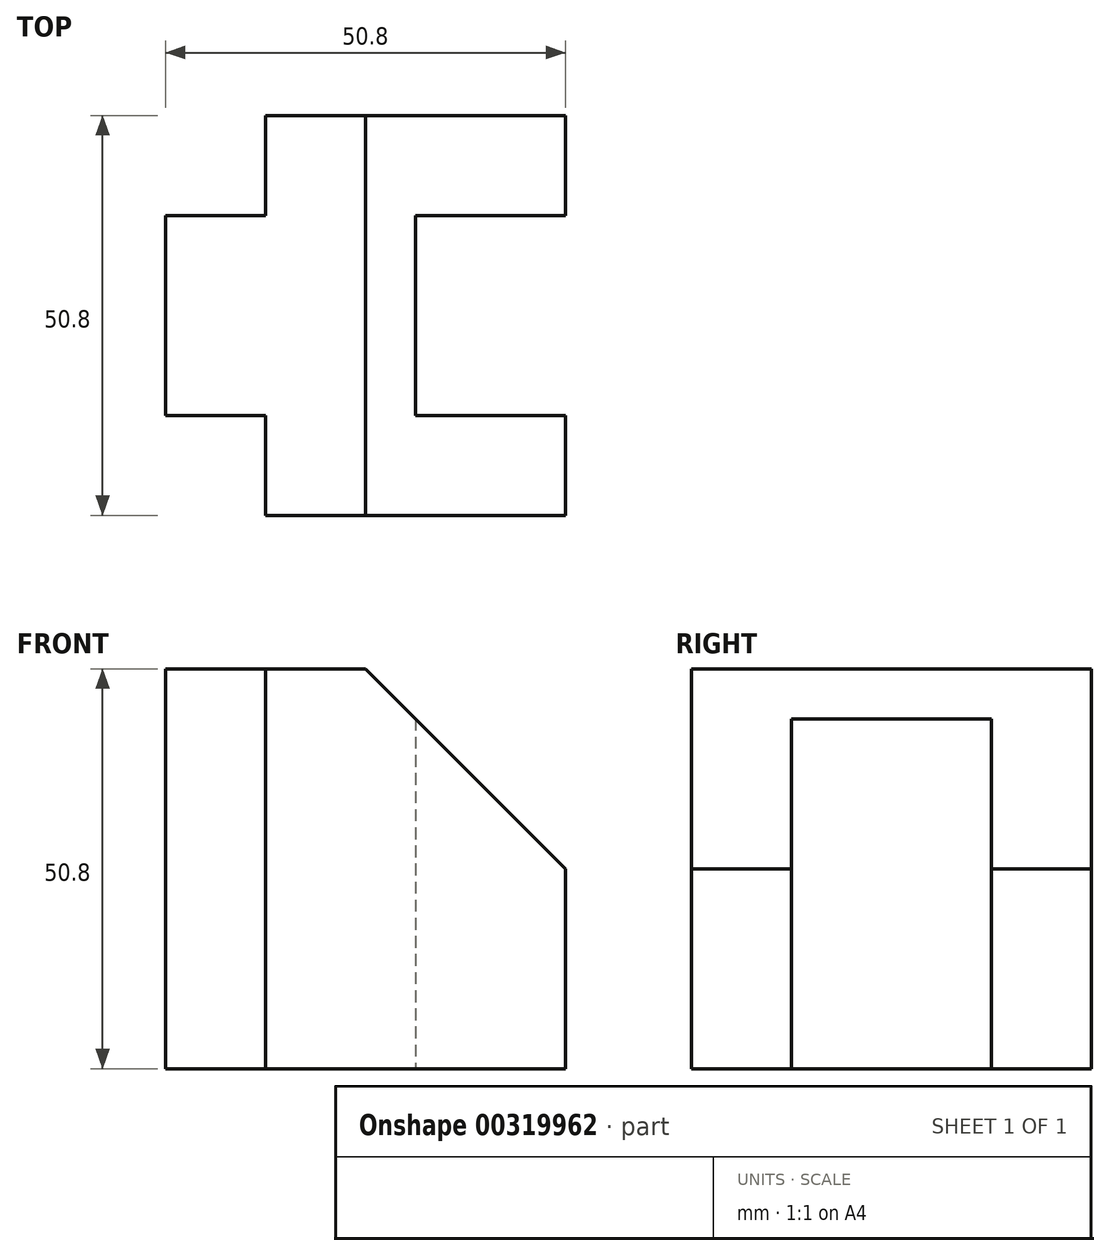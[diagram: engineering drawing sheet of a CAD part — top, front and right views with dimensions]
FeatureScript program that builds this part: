
annotation { "Feature Type Name" : "Feature", "Feature Type Description" : "" }
export const myFeature = defineFeature(function(context is Context, id is Id, definition is map)
    precondition{}
    {
        {
            var Q0;
            Q0=qCreatedBy(makeId("Top.planeOp"),FACE);
            var sketch = newSketch(context, id + "F0", { "sketchPlane" : qUnion([Q0])});
            skLineSegment(sketch, "E0", {"start": v(-19.05, 25.4) * mm, "end": v(-19.05, 12.7) * mm});
            skLineSegment(sketch, "E1", {"start": v(-19.05, 12.7) * mm, "end": v(-31.75, 12.7) * mm});
            skLineSegment(sketch, "E2", {"start": v(-31.75, 12.7) * mm, "end": v(-31.75, -12.7) * mm});
            skLineSegment(sketch, "E3", {"start": v(-31.75, -12.7) * mm, "end": v(-19.05, -12.7) * mm});
            skLineSegment(sketch, "E4", {"start": v(-19.05, -12.7) * mm, "end": v(-19.05, -25.4) * mm});
            skLineSegment(sketch, "E5", {"start": v(-19.05, -25.4) * mm, "end": v(19.05, -25.4) * mm});
            skLineSegment(sketch, "E6", {"start": v(19.05, -25.4) * mm, "end": v(19.05, -12.7) * mm});
            skLineSegment(sketch, "E7", {"start": v(19.05, -12.7) * mm, "end": v(0, -12.7) * mm});
            skLineSegment(sketch, "E8", {"start": v(0, -12.7) * mm, "end": v(0, 12.7) * mm});
            skLineSegment(sketch, "E9", {"start": v(0, 12.7) * mm, "end": v(19.05, 12.7) * mm});
            skLineSegment(sketch, "E10", {"start": v(19.05, 12.7) * mm, "end": v(19.05, 25.4) * mm});
            skLineSegment(sketch, "E11", {"start": v(19.05, 25.4) * mm, "end": v(-19.05, 25.4) * mm});
            skSolve(sketch);
        }
        {
            var Q0;
            Q0 = qSketchRegion(id + "F0", true);
            extrude(context, id + "F1", {"entities" : qUnion([Q0]), "depth" : 50.8 * mm});
        }
        {
            var Q0;
            Q0=makeQuery(id+"F1.opExtrude","SWEPT_FACE",FACE,{"disambiguationData":[OSD([sQuery(id+"F0.wireOp",EDGE,"E5")])]});
            var sketch = newSketch(context, id + "F2", { "sketchPlane" : qUnion([Q0])});
            skSolve(sketch);
        }
        {
            var Q0;
            {var subQ0=sQuery(id+"F0.wireOp",EDGE,"E5");Q0=makeQuery(id+"F2.imprint","IMPRINT",FACE,{"disambiguationData":[TD([[makeQuery(id+"F2.imprint","IMPRINT",EDGE,{"derivedFrom":makeQuery(id+"F1.opExtrude","CAP_EDGE",EDGE,{"disambiguationData":[OSD([subQ0])],"isStart":true})}),1.0]])]});}
            var sketch = newSketch(context, id + "F3", { "sketchPlane" : qUnion([Q0])});
            skLineSegment(sketch, "E12", {"start": v(19.05, 25.4) * mm, "end": v(19.05, 50.8) * mm});
            skLineSegment(sketch, "E13", {"start": v(19.05, 50.8) * mm, "end": v(-6.35, 50.8) * mm});
            skLineSegment(sketch, "E14", {"start": v(-6.35, 50.8) * mm, "end": v(19.05, 25.4) * mm});
            skSolve(sketch);
        }
        {
            var Q0;
            Q0 = qSketchRegion(id + "F3", true);
            extrude(context, id + "F4", {"entities" : qUnion([Q0]), "operationType" : NewBodyOperationType.REMOVE, "oppositeDirection" : true, "depth" : 105.16 * mm});
        }
    });
